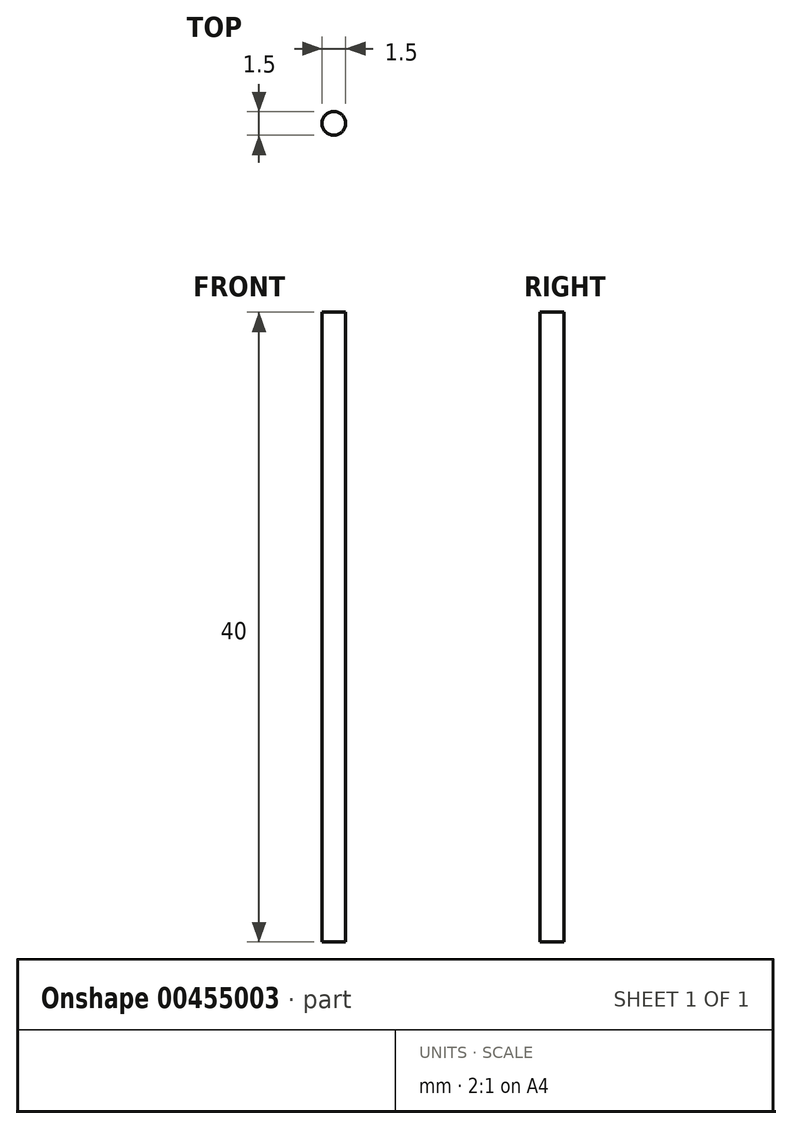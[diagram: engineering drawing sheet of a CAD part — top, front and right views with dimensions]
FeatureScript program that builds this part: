
annotation { "Feature Type Name" : "Feature", "Feature Type Description" : "" }
export const myFeature = defineFeature(function(context is Context, id is Id, definition is map)
    precondition{}
    {
        {
            var Q0;
            Q0=qCreatedBy(makeId("Top.planeOp"),FACE);
            var sketch = newSketch(context, id + "F0", { "sketchPlane" : qUnion([Q0])});
            skCircle(sketch, "E0", {"center": v(-12.63, 35.47) * mm, "radius": 0.75 * mm});
            skSolve(sketch);
        }
        {
            var Q0;
            Q0=sQuery(id+"F0.wireOp",EDGE,"E0");
            extrude(context, id + "F1", {"bodyType" : ToolBodyType.SURFACE, "surfaceEntities" : qUnion([Q0]), "depth" : 40 * mm});
        }
    });
